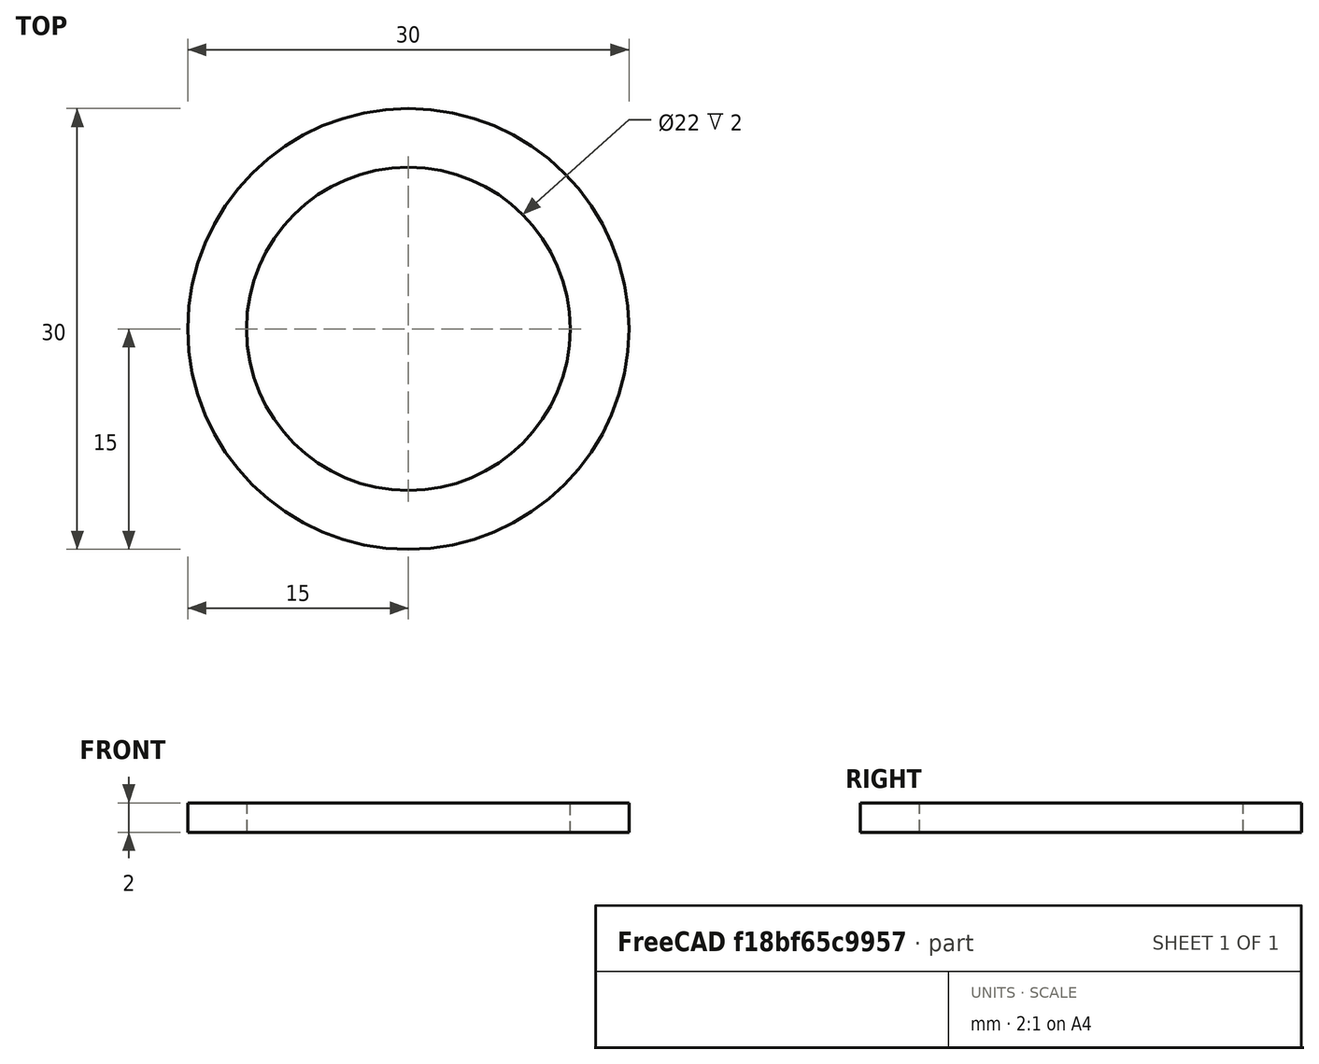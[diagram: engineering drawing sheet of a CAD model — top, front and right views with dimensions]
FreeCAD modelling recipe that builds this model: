
FCSTD DOCUMENT  (FreeCAD 0.19R24276 (Git))
Label: Rolik_6__part_2__out_print
License: All rights reserved
LicenseURL: http://en.wikipedia.org/wiki/All_rights_reserved
objects: Sketcher::SketchObject×1, PartDesign::Pad×1, PartDesign::Body×1
note: 4 computed .brp shape members not serialized (recipe doc carries the construction recipe); baked Part::Feature solids carry a one-line shape summary decoded from their .brp

FEATURE [Sketcher::SketchObject] Sketch
  FullyConstrained = true
  MapMode = 5
  Support = -> [XY_Plane]
  sketch-geometry (2):
    g0: Circle CenterX=0 CenterY=0 CenterZ=0 NormalX=0 NormalY=0 NormalZ=1 AngleXU=0 Radius=11
    g1: Circle CenterX=0 CenterY=0 CenterZ=0 NormalX=0 NormalY=0 NormalZ=1 AngleXU=0 Radius=15
  constraints (4):
    c: Coincident(g0,g-1)
    c: Coincident(g1,g0)
    c: Diameter(g0) = 22
    c: Diameter(g1) = 30
FEATURE [PartDesign::Pad] Pad
  Direction = (1,1,1)
  Length = 2
  Length2 = 100
  Profile = -> Sketch
  Type = 0
FEATURE [PartDesign::Body] Body
  Group = -> [Sketch,Pad]
  Origin = -> Origin
  Tip = -> Pad
